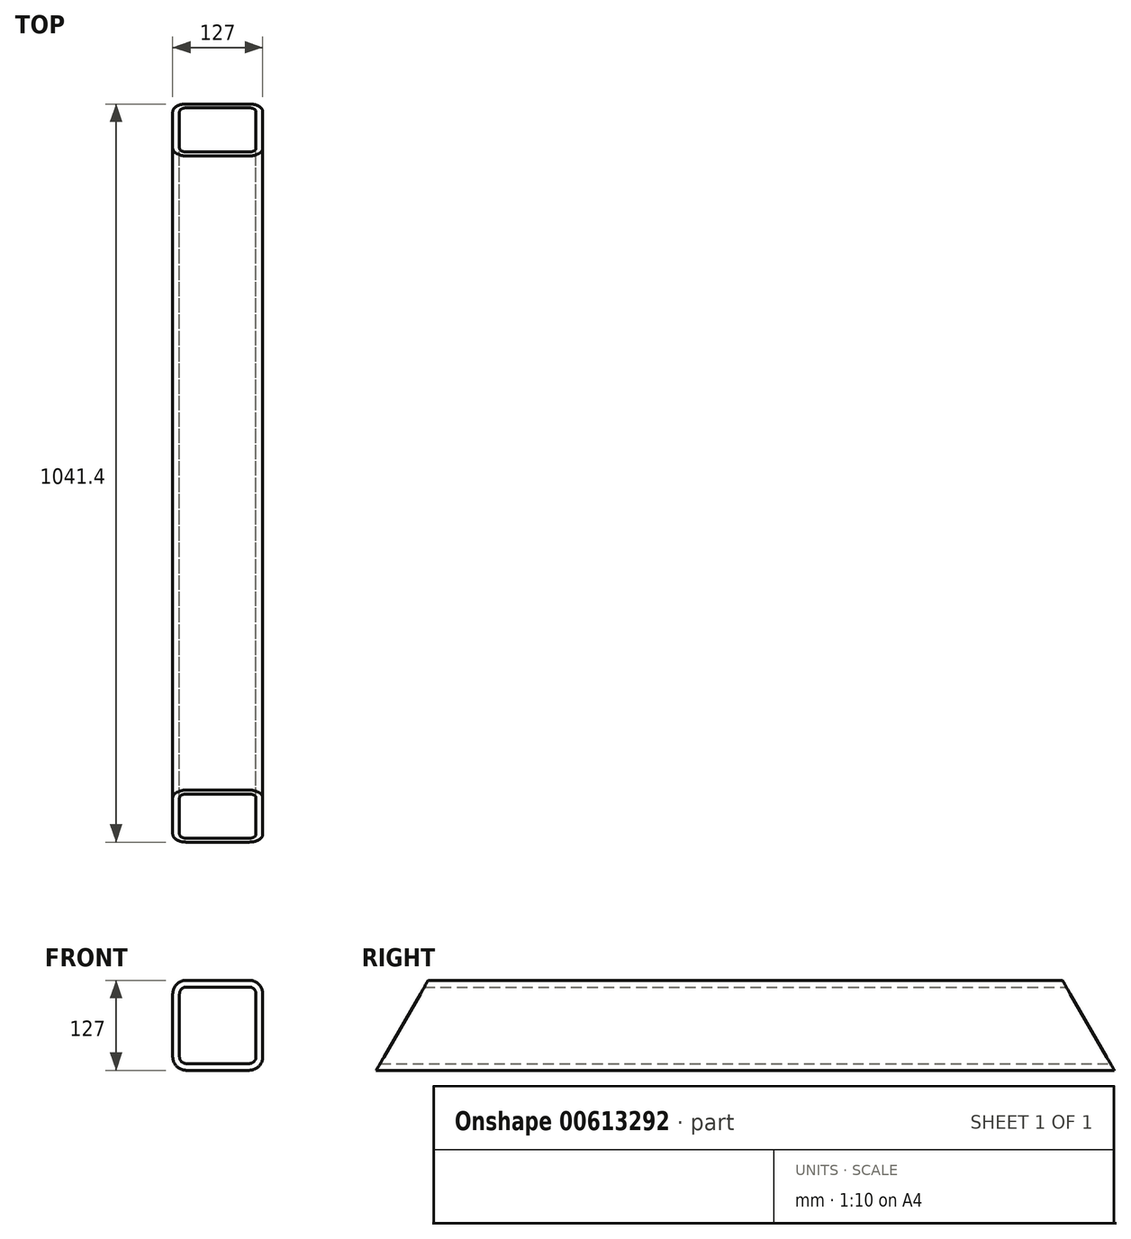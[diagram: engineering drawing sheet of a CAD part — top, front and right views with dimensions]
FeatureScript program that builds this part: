
annotation { "Feature Type Name" : "Feature", "Feature Type Description" : "" }
export const myFeature = defineFeature(function(context is Context, id is Id, definition is map)
    precondition{}
    {
        {
            var Q0;
            Q0=qCreatedBy(makeId("Front.planeOp"),FACE);
            var sketch = newSketch(context, id + "F0", { "sketchPlane" : qUnion([Q0])});
            skLineSegment(sketch, "E0.bottom", {"start": v(19.05, 0) * mm, "end": v(107.95, 0) * mm});
            skLineSegment(sketch, "E0.top", {"start": v(19.05, 127) * mm, "end": v(107.95, 127) * mm});
            skLineSegment(sketch, "E0.left", {"start": v(0, 19.05) * mm, "end": v(0, 107.95) * mm});
            skLineSegment(sketch, "E0.right", {"start": v(127, 19.05) * mm, "end": v(127, 107.95) * mm});
            skPoint(sketch, "E1.visualSharp", {"position": v(0, 127) * mm});
            skArc(sketch, "E1.filletArc", {"start": v(19.05, 127) * mm, "mid": v(5.58, 121.42) * mm, "end": v(0, 107.95) * mm});
            skPoint(sketch, "E2.visualSharp", {"position": v(127, 127) * mm});
            skArc(sketch, "E2.filletArc", {"start": v(127, 107.95) * mm, "mid": v(121.42, 121.42) * mm, "end": v(107.95, 127) * mm});
            skPoint(sketch, "E3.visualSharp", {"position": v(127, 0) * mm});
            skArc(sketch, "E3.filletArc", {"start": v(107.95, 0) * mm, "mid": v(121.42, 5.58) * mm, "end": v(127, 19.05) * mm});
            skPoint(sketch, "E4.visualSharp", {"position": v(0, 0) * mm});
            skArc(sketch, "E4.filletArc", {"start": v(0, 19.05) * mm, "mid": v(5.58, 5.58) * mm, "end": v(19.05, 0) * mm});
            skLineSegment(sketch, "E5.0", {"start": v(9.53, 19.05) * mm, "end": v(9.53, 107.95) * mm});
            skArc(sketch, "E5.1", {"start": v(19.05, 117.48) * mm, "mid": v(12.31, 114.69) * mm, "end": v(9.53, 107.95) * mm});
            skArc(sketch, "E5.2", {"start": v(9.53, 19.05) * mm, "mid": v(12.31, 12.31) * mm, "end": v(19.05, 9.53) * mm});
            skLineSegment(sketch, "E5.3", {"start": v(19.05, 117.47) * mm, "end": v(107.95, 117.47) * mm});
            skLineSegment(sketch, "E5.4", {"start": v(19.05, 9.52) * mm, "end": v(107.95, 9.52) * mm});
            skArc(sketch, "E5.5", {"start": v(107.95, 9.52) * mm, "mid": v(114.69, 12.31) * mm, "end": v(117.48, 19.05) * mm});
            skLineSegment(sketch, "E5.6", {"start": v(117.48, 19.05) * mm, "end": v(117.48, 107.95) * mm});
            skArc(sketch, "E5.7", {"start": v(117.48, 107.95) * mm, "mid": v(114.69, 114.69) * mm, "end": v(107.95, 117.48) * mm});
            skSolve(sketch);
        }
        {
            var Q0;
            Q0=makeQuery(id+"F0.imprint","IMPRINT",FACE,{"disambiguationData":[TD([[makeQuery(id+"F0.imprint","IMPRINT",EDGE,{"derivedFrom":sQuery(id+"F0.wireOp",EDGE,"1qnOmSaI-Xxrh-0afN-UeiG-LIwPmX5NAdLk.bottom")}),1.0]])]});
            var Q1;
            Q1=makeQuery(id+"F0.imprint","IMPRINT",FACE,{"disambiguationData":[TD([[makeQuery(id+"F0.imprint","IMPRINT",EDGE,{"derivedFrom":sQuery(id+"F0.wireOp",EDGE,"4ba0bba3-8742-4700-8735-c76f5317d59b.0.1.0")}),1.0]])]});
            var Q2;
            Q2=makeQuery(id+"F0.imprint","IMPRINT",FACE,{"disambiguationData":[TD([[makeQuery(id+"F0.imprint","IMPRINT",EDGE,{"derivedFrom":sQuery(id+"F0.wireOp",EDGE,"4ba0bba3-8742-4700-8735-c76f5317d59b.1.1.0")}),1.0]])]});
            var Q3;
            Q3=makeQuery(id+"F0.imprint","IMPRINT",FACE,{"disambiguationData":[TD([[makeQuery(id+"F0.imprint","IMPRINT",EDGE,{"derivedFrom":sQuery(id+"F0.wireOp",EDGE,"4ba0bba3-8742-4700-8735-c76f5317d59b.1.0.0")}),1.0]])]});
            var Q4;
            Q4=makeQuery(id+"F0.imprint","IMPRINT",FACE,{"disambiguationData":[TD([[makeQuery(id+"F0.imprint","IMPRINT",EDGE,{"derivedFrom":sQuery(id+"F0.wireOp",EDGE,"E0.bottom")}),1.0]])]});
            var Q5;
            Q5=makeQuery(id+"F0.imprint","IMPRINT",FACE,{"disambiguationData":[TD([[makeQuery(id+"F0.imprint","IMPRINT",EDGE,{"derivedFrom":sQuery(id+"F0.wireOp",EDGE,"bJ1m94SH-JbWV-fS9y-Xvgq-A2zdKJ9BKWsM")}),1.0]])]});
            extrude(context, id + "F1", {"entities" : qUnion([Q0, Q1, Q2, Q3, Q4, Q5]), "depth" : 1041.4 * mm, "offsetDistance" : 25.4 * mm});
        }
        {
            var Q0;
            Q0=qCreatedBy(makeId("Right.planeOp"),FACE);
            var sketch = newSketch(context, id + "F2", { "sketchPlane" : qUnion([Q0])});
            skLineSegment(sketch, "E6.0", {"start": v(-1041.4, 0) * mm, "end": v(0, 0) * mm});
            skLineSegment(sketch, "E6.1", {"start": v(-1041.4, 127) * mm, "end": v(0, 127) * mm});
            skLineSegment(sketch, "E6.2", {"start": v(-1041.4, 127) * mm, "end": v(-1041.4, 107.95) * mm});
            skLineSegment(sketch, "E6.3", {"start": v(-1041.4, 19.05) * mm, "end": v(-1041.4, 107.95) * mm});
            skLineSegment(sketch, "E6.4", {"start": v(-1041.4, 19.05) * mm, "end": v(-1041.4, 0) * mm});
            skLineSegment(sketch, "E6.5", {"start": v(0, 19.05) * mm, "end": v(0, 0) * mm});
            skLineSegment(sketch, "E6.6", {"start": v(0, 19.05) * mm, "end": v(0, 107.95) * mm});
            skLineSegment(sketch, "E6.7", {"start": v(0, 127) * mm, "end": v(0, 107.95) * mm});
            skLineSegment(sketch, "E7", {"start": v(-1041.4, 0) * mm, "end": v(-968.08, 127) * mm});
            skLineSegment(sketch, "E8", {"start": v(0, 0) * mm, "end": v(-73.32, 127) * mm});
            skSolve(sketch);
        }
        {
            var Q0;
            {var subQ0=sQuery(id+"F2.wireOp",EDGE,"E6.2");Q0=makeQuery(id+"F2.imprint","IMPRINT",FACE,{"disambiguationData":[TD([[makeQuery(id+"F2.imprint","IMPRINT",EDGE,{"derivedFrom":subQ0}),1.0]])]});}
            var Q1;
            Q1=makeQuery(id+"F2.imprint","IMPRINT",FACE,{"disambiguationData":[TD([[makeQuery(id+"F2.imprint","IMPRINT",EDGE,{"derivedFrom":sQuery(id+"F2.wireOp",EDGE,"E6.5")}),-1.0]])]});
            extrude(context, id + "F3", {"entities" : qUnion([Q0, Q1]), "operationType" : NewBodyOperationType.REMOVE, "endBound" : BoundingType.THROUGH_ALL, "depth" : 25.4 * mm, "offsetDistance" : 25.4 * mm});
        }
    });
